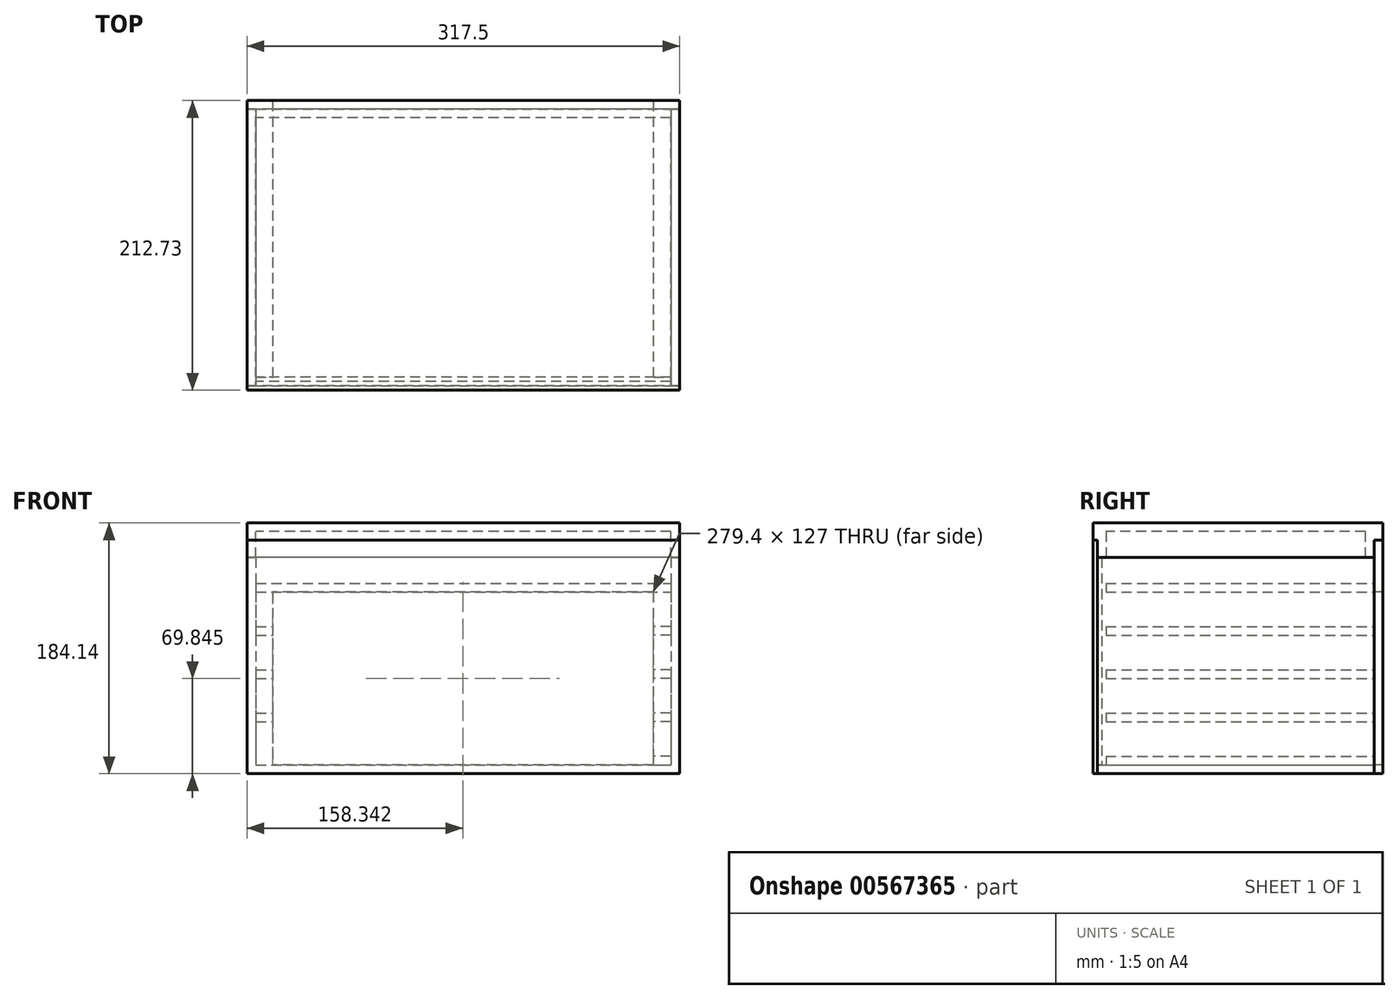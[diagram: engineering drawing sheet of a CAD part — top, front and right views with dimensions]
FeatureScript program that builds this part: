
annotation { "Feature Type Name" : "Feature", "Feature Type Description" : "" }
export const myFeature = defineFeature(function(context is Context, id is Id, definition is map)
    precondition{}
    {
        {
            var Q0;
            Q0=qCreatedBy(makeId("Front.planeOp"),FACE);
            var sketch = newSketch(context, id + "F0", { "sketchPlane" : qUnion([Q0])});
            skLineSegment(sketch, "E0.bottom", {"start": v(-158.75, 85.73) * mm, "end": v(158.75, 85.73) * mm});
            skLineSegment(sketch, "E0.top", {"start": v(-158.75, -85.72) * mm, "end": v(158.75, -85.72) * mm});
            skLineSegment(sketch, "E0.left", {"start": v(-158.75, 85.73) * mm, "end": v(-158.75, -85.72) * mm});
            skLineSegment(sketch, "E0.right", {"start": v(158.75, 85.73) * mm, "end": v(158.75, -85.72) * mm});
            skPoint(sketch, "E0.middle", {"position": v(0, 0) * mm});
            skLineSegment(sketch, "E1.0", {"start": v(-152.4, 79.38) * mm, "end": v(152.4, 79.38) * mm});
            skLineSegment(sketch, "E1.1", {"start": v(-152.4, 79.38) * mm, "end": v(-152.4, -79.38) * mm});
            skLineSegment(sketch, "E1.2", {"start": v(-152.4, -79.38) * mm, "end": v(152.4, -79.38) * mm});
            skLineSegment(sketch, "E1.3", {"start": v(152.4, 79.38) * mm, "end": v(152.4, -79.38) * mm});
            skLineSegment(sketch, "E2.0", {"start": v(-158.75, 85.73) * mm, "end": v(-158.75, -79.37) * mm});
            skLineSegment(sketch, "E3", {"start": v(-152.4, 53.98) * mm, "end": v(152.4, 53.98) * mm});
            skLineSegment(sketch, "E4.bottom", {"start": v(-152.4, -79.38) * mm, "end": v(-139.7, -79.38) * mm});
            skLineSegment(sketch, "E4.top", {"start": v(-152.4, -73.03) * mm, "end": v(-139.7, -73.03) * mm});
            skLineSegment(sketch, "E4.left", {"start": v(-152.4, -79.38) * mm, "end": v(-152.4, -73.03) * mm});
            skLineSegment(sketch, "E4.right", {"start": v(-139.7, -79.38) * mm, "end": v(-139.7, -73.03) * mm});
            skLineSegment(sketch, "E5.MirrorCS", {"start": v(152.4, -73.03) * mm, "end": v(139.7, -73.03) * mm});
            skLineSegment(sketch, "E6.MirrorCS", {"start": v(139.7, -79.38) * mm, "end": v(139.7, -73.03) * mm});
            skLineSegment(sketch, "E7.MirrorCS", {"start": v(152.4, -79.38) * mm, "end": v(139.7, -79.38) * mm});
            skLineSegment(sketch, "E8.0.1.0", {"start": v(-152.4, -41.28) * mm, "end": v(-139.7, -41.28) * mm});
            skLineSegment(sketch, "E8.0.1.1", {"start": v(-139.7, -47.63) * mm, "end": v(-139.7, -41.28) * mm});
            skLineSegment(sketch, "E8.0.1.2", {"start": v(-152.4, -47.63) * mm, "end": v(-139.7, -47.63) * mm});
            skLineSegment(sketch, "E8.0.2.0", {"start": v(-152.4, -9.53) * mm, "end": v(-139.7, -9.53) * mm});
            skLineSegment(sketch, "E8.0.2.1", {"start": v(-139.7, -15.88) * mm, "end": v(-139.7, -9.53) * mm});
            skLineSegment(sketch, "E8.0.2.2", {"start": v(-152.4, -15.88) * mm, "end": v(-139.7, -15.88) * mm});
            skLineSegment(sketch, "E8.direction1", {"start": v(-152.4, -79.38) * mm, "end": v(-117.86, -79.12) * mm, "construction": true});
            skLineSegment(sketch, "E8.direction2", {"start": v(-152.4, -79.38) * mm, "end": v(-152.4, -47.63) * mm, "construction": true});
            skLineSegment(sketch, "E9.MirrorCS", {"start": v(152.4, -79.38) * mm, "end": v(117.86, -79.12) * mm, "construction": true});
            skLineSegment(sketch, "E10.MirrorCS", {"start": v(152.4, -79.38) * mm, "end": v(152.4, -47.63) * mm, "construction": true});
            skLineSegment(sketch, "E11.MirrorCS", {"start": v(152.4, -47.62) * mm, "end": v(139.7, -47.62) * mm});
            skLineSegment(sketch, "E12.MirrorCS", {"start": v(139.7, -47.63) * mm, "end": v(139.7, -41.28) * mm});
            skLineSegment(sketch, "E13.MirrorCS", {"start": v(152.4, -41.28) * mm, "end": v(139.7, -41.28) * mm});
            skLineSegment(sketch, "E14.MirrorCS", {"start": v(152.4, -15.88) * mm, "end": v(139.7, -15.88) * mm});
            skLineSegment(sketch, "E15.MirrorCS", {"start": v(139.7, -15.88) * mm, "end": v(139.7, -9.53) * mm});
            skLineSegment(sketch, "E16.MirrorCS", {"start": v(152.4, -9.53) * mm, "end": v(139.7, -9.53) * mm});
            skLineSegment(sketch, "E17.0", {"start": v(-152.4, 47.63) * mm, "end": v(152.4, 47.63) * mm});
            skLineSegment(sketch, "E18.0.0.3", {"start": v(-152.4, 22.22) * mm, "end": v(-139.7, 22.22) * mm});
            skLineSegment(sketch, "E18.3.0.3", {"start": v(-139.7, 15.87) * mm, "end": v(-139.7, 22.22) * mm});
            skLineSegment(sketch, "E18.6.0.3", {"start": v(-152.4, 15.87) * mm, "end": v(-139.7, 15.87) * mm});
            skLineSegment(sketch, "E19.MirrorCS", {"start": v(152.4, 22.22) * mm, "end": v(139.7, 22.22) * mm});
            skLineSegment(sketch, "E20.MirrorCS", {"start": v(139.7, 15.87) * mm, "end": v(139.7, 22.22) * mm});
            skLineSegment(sketch, "E21.MirrorCS", {"start": v(152.4, 15.87) * mm, "end": v(139.7, 15.87) * mm});
            skSolve(sketch);
        }
        {
            var Q0;
            {var subQ19=sQuery(id+"F0.wireOp",EDGE,"E0.bottom");Q0=makeQuery(id+"F0.imprint","IMPRINT",FACE,{"disambiguationData":[TD([[makeQuery(id+"F0.imprint","IMPRINT",EDGE,{"derivedFrom":subQ19}),-1.0]])]});}
            extrude(context, id + "F1", {"entities" : qUnion([Q0]), "depth" : 203.2 * mm, "offsetDistance" : 25.4 * mm});
        }
        {
            var Q0;
            {var subQ0=sQuery(id+"F0.wireOp",EDGE,"E3");Q0=makeQuery(id+"F0.imprint","IMPRINT",FACE,{"disambiguationData":[TD([[makeQuery(id+"F0.imprint","IMPRINT",EDGE,{"derivedFrom":subQ0}),-1.0]])]});}
            var Q1;
            {var subQ0=sQuery(id+"F0.wireOp",EDGE,"E8.0.2.0");Q1=makeQuery(id+"F0.imprint","IMPRINT",FACE,{"disambiguationData":[TD([[makeQuery(id+"F0.imprint","IMPRINT",EDGE,{"derivedFrom":subQ0}),-1.0]])]});}
            var Q2;
            {var subQ0=sQuery(id+"F0.wireOp",EDGE,"E8.0.1.0");Q2=makeQuery(id+"F0.imprint","IMPRINT",FACE,{"disambiguationData":[TD([[makeQuery(id+"F0.imprint","IMPRINT",EDGE,{"derivedFrom":subQ0}),-1.0]])]});}
            var Q3;
            Q3=makeQuery(id+"F0.imprint","IMPRINT",FACE,{"disambiguationData":[TD([[makeQuery(id+"F0.imprint","IMPRINT",EDGE,{"derivedFrom":sQuery(id+"F0.wireOp",EDGE,"E4.bottom")}),1.0]])]});
            var Q4;
            {var subQ0=sQuery(id+"F0.wireOp",EDGE,"E5.MirrorCS");Q4=makeQuery(id+"F0.imprint","IMPRINT",FACE,{"disambiguationData":[TD([[makeQuery(id+"F0.imprint","IMPRINT",EDGE,{"derivedFrom":subQ0}),1.0]])]});}
            var Q5;
            {var subQ0=sQuery(id+"F0.wireOp",EDGE,"E11.MirrorCS");Q5=makeQuery(id+"F0.imprint","IMPRINT",FACE,{"disambiguationData":[TD([[makeQuery(id+"F0.imprint","IMPRINT",EDGE,{"derivedFrom":subQ0}),-1.0]])]});}
            var Q6;
            {var subQ0=sQuery(id+"F0.wireOp",EDGE,"E14.MirrorCS");Q6=makeQuery(id+"F0.imprint","IMPRINT",FACE,{"disambiguationData":[TD([[makeQuery(id+"F0.imprint","IMPRINT",EDGE,{"derivedFrom":subQ0}),-1.0]])]});}
            var Q7;
            {var subQ0=sQuery(id+"F0.wireOp",EDGE,"E18.0.0.3");Q7=makeQuery(id+"F0.imprint","IMPRINT",FACE,{"disambiguationData":[TD([[makeQuery(id+"F0.imprint","IMPRINT",EDGE,{"derivedFrom":subQ0}),-1.0]])]});}
            var Q8;
            {var subQ0=sQuery(id+"F0.wireOp",EDGE,"E19.MirrorCS");Q8=makeQuery(id+"F0.imprint","IMPRINT",FACE,{"disambiguationData":[TD([[makeQuery(id+"F0.imprint","IMPRINT",EDGE,{"derivedFrom":subQ0}),1.0]])]});}
            extrude(context, id + "F2", {"entities" : qUnion([Q0, Q1, Q2, Q3, Q4, Q5, Q6, Q7, Q8]), "operationType" : NewBodyOperationType.ADD, "depth" : 196.85 * mm, "offsetDistance" : 25.4 * mm});
        }
        {
            var Q0;
            Q0=makeQuery(id+"F1.opExtrude","SWEPT_FACE",FACE,{"disambiguationData":[OSD([sQuery(id+"F0.wireOp",EDGE,"E1.2")])]});
            cPlane(context, id + "F3", {"entities" : qUnion([Q0]), "cplaneType" : CPlaneType.OFFSET, "offset" : 152.4 * mm, "width" : 152.4 * mm, "height" : 152.4 * mm});
        }
        {
            var Q0;
            Q0=makeQuery(id+"F1.opExtrude","CAP_FACE",FACE,{"disambiguationData":[OSD([sQuery(id+"F0.wireOp",EDGE,"E0.bottom"),sQuery(id+"F0.wireOp",EDGE,"E0.top"),sQuery(id+"F0.wireOp",EDGE,"E0.left"),sQuery(id+"F0.wireOp",EDGE,"E0.right"),sQuery(id+"F0.wireOp",EDGE,"E1.0"),sQuery(id+"F0.wireOp",EDGE,"E1.1"),sQuery(id+"F0.wireOp",EDGE,"E1.2"),sQuery(id+"F0.wireOp",EDGE,"E1.3"),sQuery(id+"F0.wireOp",EDGE,"E2.0"),sQuery(id+"F0.wireOp",EDGE,"E4.left")])],"isStart":false});
            cPlane(context, id + "F4", {"entities" : qUnion([Q0]), "cplaneType" : CPlaneType.OFFSET, "offset" : 0 * mm, "width" : 152.4 * mm, "height" : 152.4 * mm});
        }
        {
            var Q0;
            Q0=qCreatedBy(id+"F4.planeOp",FACE);
            var sketch = newSketch(context, id + "F5", { "sketchPlane" : qUnion([Q0])});
            skLineSegment(sketch, "E22.bottom", {"start": v(-158.75, 85.73) * mm, "end": v(158.75, 85.73) * mm});
            skLineSegment(sketch, "E22.top", {"start": v(-158.75, -85.72) * mm, "end": v(158.75, -85.72) * mm});
            skLineSegment(sketch, "E22.left", {"start": v(-158.75, 85.73) * mm, "end": v(-158.75, -85.72) * mm});
            skLineSegment(sketch, "E22.right", {"start": v(158.75, 85.73) * mm, "end": v(158.75, -85.72) * mm});
            skLineSegment(sketch, "E23.0", {"start": v(-152.4, 79.37) * mm, "end": v(152.4, 79.37) * mm});
            skLineSegment(sketch, "E23.1", {"start": v(-152.4, 79.37) * mm, "end": v(-152.4, -79.37) * mm});
            skLineSegment(sketch, "E23.2", {"start": v(-152.4, -79.37) * mm, "end": v(152.4, -79.37) * mm});
            skLineSegment(sketch, "E23.3", {"start": v(152.4, 79.37) * mm, "end": v(152.4, -79.37) * mm});
            skSolve(sketch);
        }
        {
            var Q0;
            Q0 = qSketchRegion(id + "F5", true);
            var Q1;
            Q1=makeQuery(id+"F5.imprint","IMPRINT",FACE,{"disambiguationData":[TD([[makeQuery(id+"F5.imprint","IMPRINT",EDGE,{"derivedFrom":sQuery(id+"F5.wireOp",EDGE,"E23.0")}),-1.0]])]});
            extrude(context, id + "F6", {"entities" : qUnion([Q0, Q1]), "depth" : 3.17 * mm, "offsetDistance" : 25.4 * mm});
        }
        {
            var Q0;
            {var subQ20=sQuery(id+"F0.wireOp",EDGE,"E0.bottom");Q0=makeQuery(id+"F0.imprint","IMPRINT",FACE,{"disambiguationData":[TD([[makeQuery(id+"F0.imprint","IMPRINT",EDGE,{"derivedFrom":subQ20}),-1.0]])]});}
            cPlane(context, id + "F7", {"entities" : qUnion([Q0]), "cplaneType" : CPlaneType.OFFSET, "offset" : 0 * mm, "width" : 152.4 * mm, "height" : 152.4 * mm});
        }
        {
            var Q0;
            Q0=qCreatedBy(id+"F7.planeOp",FACE);
            var sketch = newSketch(context, id + "F8", { "sketchPlane" : qUnion([Q0])});
            skLineSegment(sketch, "E24.bottom", {"start": v(158.75, 85.73) * mm, "end": v(-158.75, 85.72) * mm});
            skLineSegment(sketch, "E24.top", {"start": v(158.75, -85.72) * mm, "end": v(-158.75, -85.73) * mm});
            skLineSegment(sketch, "E24.left", {"start": v(158.75, 85.73) * mm, "end": v(158.75, -85.72) * mm});
            skLineSegment(sketch, "E24.right", {"start": v(-158.75, 85.73) * mm, "end": v(-158.75, -85.73) * mm});
            skLineSegment(sketch, "E25.2", {"start": v(139.3, -79.38) * mm, "end": v(-140.1, -79.38) * mm});
            skLineSegment(sketch, "E26", {"start": v(139.3, 47.63) * mm, "end": v(-140.1, 47.63) * mm});
            skLineSegment(sketch, "E27", {"start": v(139.3, 47.63) * mm, "end": v(139.3, -79.38) * mm});
            skLineSegment(sketch, "E28", {"start": v(-140.1, 47.63) * mm, "end": v(-140.1, -79.38) * mm});
            skSolve(sketch);
        }
        {
            var Q0;
            Q0=makeQuery(id+"F8.imprint","IMPRINT",FACE,{"disambiguationData":[TD([[makeQuery(id+"F8.imprint","IMPRINT",EDGE,{"derivedFrom":sQuery(id+"F8.wireOp",EDGE,"E24.bottom")}),1.0]])]});
            extrude(context, id + "F9", {"entities" : qUnion([Q0]), "oppositeDirection" : true, "depth" : 6.35 * mm, "offsetDistance" : 25.4 * mm});
        }
        {
            var Q0;
            Q0=makeQuery(id+"F5.imprint","IMPRINT",FACE,{"disambiguationData":[TD([[makeQuery(id+"F5.imprint","IMPRINT",EDGE,{"derivedFrom":sQuery(id+"F5.wireOp",EDGE,"E23.0")}),-1.0]])]});
            extrude(context, id + "F10", {"entities" : qUnion([Q0]), "oppositeDirection" : true, "depth" : 3.17 * mm, "offsetDistance" : 25.4 * mm});
        }
        {
            var Q0;
            Q0=qCreatedBy(id+"F3.planeOp",FACE);
            var sketch = newSketch(context, id + "F11", { "sketchPlane" : qUnion([Q0])});
            skLineSegment(sketch, "E29.bottom", {"start": v(-158.75, 0) * mm, "end": v(158.75, 0) * mm});
            skLineSegment(sketch, "E29.top", {"start": v(-158.75, -203.2) * mm, "end": v(158.75, -203.2) * mm});
            skLineSegment(sketch, "E29.left", {"start": v(-158.75, 0) * mm, "end": v(-158.75, -203.2) * mm});
            skLineSegment(sketch, "E29.right", {"start": v(158.75, 0) * mm, "end": v(158.75, -203.2) * mm});
            skSolve(sketch);
        }
        {
            var Q0;
            Q0 = qSketchRegion(id + "F11", true);
            extrude(context, id + "F12", {"entities" : qUnion([Q0]), "operationType" : NewBodyOperationType.REMOVE, "depth" : 25.4 * mm, "offsetDistance" : 25.4 * mm});
        }
        {
            var Q0;
            Q0=makeQuery(id+"F1.opExtrude","SWEPT_FACE",FACE,{"disambiguationData":[OSD([sQuery(id+"F0.wireOp",EDGE,"E0.left"),sQuery(id+"F0.wireOp",EDGE,"E2.0")])]});
            cPlane(context, id + "F13", {"entities" : qUnion([Q0]), "cplaneType" : CPlaneType.OFFSET, "offset" : 0 * mm, "width" : 152.4 * mm, "height" : 152.4 * mm});
        }
        {
            var Q0;
            Q0=qCreatedBy(id+"F13.planeOp",FACE);
            var sketch = newSketch(context, id + "F14", { "sketchPlane" : qUnion([Q0])});
            skLineSegment(sketch, "E30", {"start": v(-6.35, 85.72) * mm, "end": v(-6.35, 98.43) * mm});
            skLineSegment(sketch, "E31", {"start": v(-6.35, 98.43) * mm, "end": v(206.38, 98.43) * mm});
            skLineSegment(sketch, "E32", {"start": v(206.38, 98.43) * mm, "end": v(206.38, 85.72) * mm});
            skLineSegment(sketch, "E33", {"start": v(206.38, 85.72) * mm, "end": v(203.2, 85.72) * mm});
            skLineSegment(sketch, "E34", {"start": v(203.2, 85.72) * mm, "end": v(203.2, 73.02) * mm});
            skLineSegment(sketch, "E35", {"start": v(0, 73.03) * mm, "end": v(0, 85.72) * mm});
            skLineSegment(sketch, "E36", {"start": v(0, 85.72) * mm, "end": v(-6.35, 85.72) * mm});
            skLineSegment(sketch, "E37", {"start": v(6.35, 73.02) * mm, "end": v(6.35, 98.43) * mm});
            skLineSegment(sketch, "E38", {"start": v(196.85, 98.43) * mm, "end": v(196.85, 73.02) * mm});
            skLineSegment(sketch, "E39", {"start": v(6.35, 92.08) * mm, "end": v(196.85, 92.08) * mm});
            skLineSegment(sketch, "E40", {"start": v(0, 73.03) * mm, "end": v(6.35, 73.02) * mm});
            skLineSegment(sketch, "E41", {"start": v(6.35, 73.02) * mm, "end": v(196.85, 73.02) * mm});
            skLineSegment(sketch, "E42", {"start": v(203.2, 73.02) * mm, "end": v(196.85, 73.02) * mm});
            skSolve(sketch);
        }
        {
            var Q0;
            Q0 = qSketchRegion(id + "F14", true);
            var Q1;
            Q1=makeQuery(id+"F1.opExtrude","SWEPT_FACE",FACE,{"disambiguationData":[OSD([sQuery(id+"F0.wireOp",EDGE,"E0.right")])]});
            var Q2;
            Q2=makeQuery(id+"F1.opExtrude","SWEPT_FACE",FACE,{"disambiguationData":[OSD([sQuery(id+"F0.wireOp",EDGE,"E0.left"),sQuery(id+"F0.wireOp",EDGE,"E2.0")])]});
            extrude(context, id + "F15", {"entities" : qUnion([Q0]), "endBound" : BoundingType.UP_TO_SURFACE, "oppositeDirection" : true, "depth" : 317.5 * mm, "endBoundEntityFace" : qUnion([Q1]), "offsetDistance" : 25.4 * mm});
        }
        {
            var Q0;
            {var subQ2=sQuery(id+"F14.wireOp",EDGE,"E39");Q0=makeQuery(id+"F14.imprint","IMPRINT",FACE,{"disambiguationData":[TD([[makeQuery(id+"F14.imprint","IMPRINT",EDGE,{"derivedFrom":subQ2}),-1.0]])]});}
            extrude(context, id + "F16", {"entities" : qUnion([Q0]), "operationType" : NewBodyOperationType.REMOVE, "oppositeDirection" : true, "depth" : 311.15 * mm, "offsetDistance" : 25.4 * mm, "hasSecondDirection" : true, "secondDirectionOppositeDirection" : true, "secondDirectionDepth" : 6.35 * mm});
        }
    });
